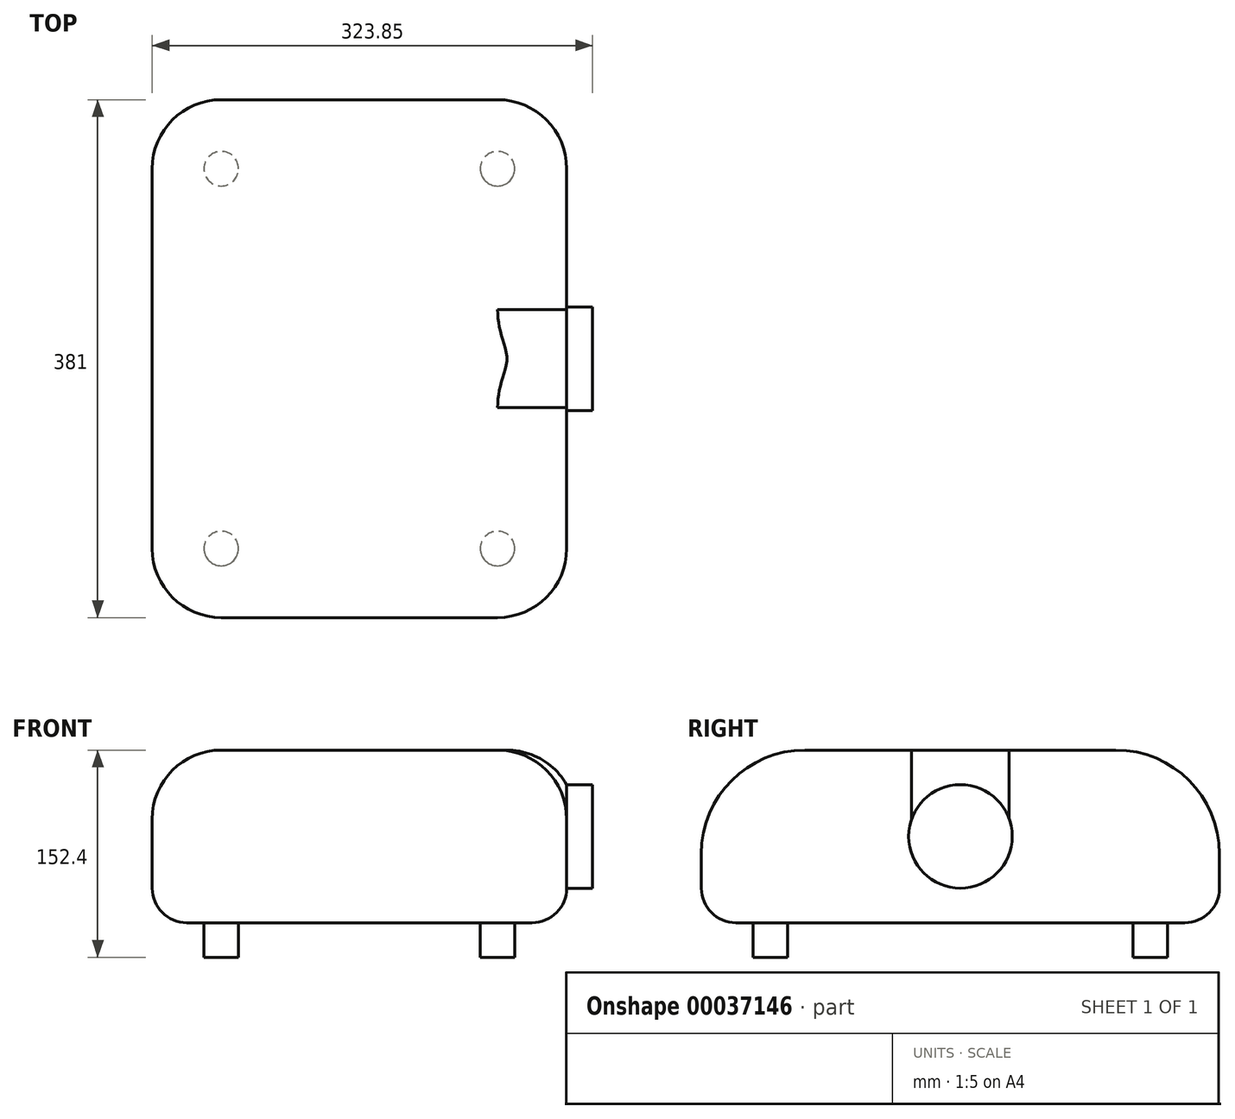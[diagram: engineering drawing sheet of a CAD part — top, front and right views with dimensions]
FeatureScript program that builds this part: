
annotation { "Feature Type Name" : "Feature", "Feature Type Description" : "" }
export const myFeature = defineFeature(function(context is Context, id is Id, definition is map)
    precondition{}
    {
        {
            var Q0;
            Q0=qCreatedBy(makeId("Top.planeOp"),FACE);
            var sketch = newSketch(context, id + "F0", { "sketchPlane" : qUnion([Q0])});
            skLineSegment(sketch, "E0.bottom", {"start": v(-168.65, 186.98) * mm, "end": v(136.15, 186.98) * mm});
            skLineSegment(sketch, "E0.top", {"start": v(-168.65, -194.02) * mm, "end": v(136.15, -194.02) * mm});
            skLineSegment(sketch, "E0.left", {"start": v(-168.65, 186.98) * mm, "end": v(-168.65, -194.02) * mm});
            skLineSegment(sketch, "E0.right", {"start": v(136.15, 186.98) * mm, "end": v(136.15, -194.02) * mm});
            skSolve(sketch);
        }
        {
            var Q0;
            Q0 = qSketchRegion(id + "F0", true);
            extrude(context, id + "F1", {"entities" : qUnion([Q0]), "depth" : 127 * mm});
        }
        {
            var Q0;
            Q0=makeQuery(id+"F1.opExtrude","CAP_FACE",FACE,{"disambiguationData":[OSD([sQuery(id+"F0.wireOp",EDGE,"E0.bottom"),sQuery(id+"F0.wireOp",EDGE,"E0.top"),sQuery(id+"F0.wireOp",EDGE,"E0.left"),sQuery(id+"F0.wireOp",EDGE,"E0.right")])],"isStart":true});
            var sketch = newSketch(context, id + "F2", { "sketchPlane" : qUnion([Q0])});
            skCircle(sketch, "E1", {"center": v(-117.85, -136.18) * mm, "radius": 12.7 * mm});
            skCircle(sketch, "E2", {"center": v(-117.85, 143.22) * mm, "radius": 12.7 * mm});
            skCircle(sketch, "E3", {"center": v(85.35, 143.22) * mm, "radius": 12.7 * mm});
            skCircle(sketch, "E4", {"center": v(85.35, -136.18) * mm, "radius": 12.7 * mm});
            skSolve(sketch);
        }
        {
            var Q0;
            Q0 = qSketchRegion(id + "F2", true);
            extrude(context, id + "F3", {"entities" : qUnion([Q0]), "operationType" : NewBodyOperationType.ADD, "depth" : 25.4 * mm});
        }
        {
            var Q0;
            Q0=makeQuery(id+"F1.opExtrude","CAP_EDGE",EDGE,{"disambiguationData":[OSD([sQuery(id+"F0.wireOp",EDGE,"E0.bottom")])],"isStart":false});
            var Q1;
            Q1=makeQuery(id+"F1.opExtrude","CAP_EDGE",EDGE,{"disambiguationData":[OSD([sQuery(id+"F0.wireOp",EDGE,"E0.top")])],"isStart":false});
            fillet(context, id + "F4", {"entities" : qUnion([Q0, Q1]), "radius" : 76.2 * mm, "tangentPropagation" : true, "allowEdgeOverflow" : false});
        }
        {
            var Q0;
            Q0=makeQuery(id+"F1.opExtrude","SWEPT_FACE",FACE,{"disambiguationData":[OSD([sQuery(id+"F0.wireOp",EDGE,"E0.right")])]});
            var sketch = newSketch(context, id + "F5", { "sketchPlane" : qUnion([Q0])});
            skCircle(sketch, "E5", {"center": v(-3.52, 63.5) * mm, "radius": 38.1 * mm});
            skPoint(sketch, "E5.centerSnap0", {"position": v(-3.52, 76.2) * mm});
            skSolve(sketch);
        }
        {
            var Q0;
            Q0 = qSketchRegion(id + "F5", true);
            extrude(context, id + "F6", {"entities" : qUnion([Q0]), "operationType" : NewBodyOperationType.ADD, "depth" : 19.05 * mm, "hasSecondDirection" : true, "secondDirectionOppositeDirection" : true, "secondDirectionDepth" : 25.4 * mm});
        }
        {
            var Q0;
            Q0=makeQuery(id+"F1.opExtrude","CAP_EDGE",EDGE,{"disambiguationData":[OSD([sQuery(id+"F0.wireOp",EDGE,"E0.right")])],"isStart":false});
            var Q1;
            Q1=makeQuery(id+"F1.opExtrude","CAP_EDGE",EDGE,{"disambiguationData":[OSD([sQuery(id+"F0.wireOp",EDGE,"E0.left")])],"isStart":false});
            fillet(context, id + "F7", {"entities" : qUnion([Q0, Q1]), "radius" : 50.8 * mm, "tangentPropagation" : true, "allowEdgeOverflow" : false});
        }
        {
            var Q0;
            Q0=makeQuery(id+"F1.opExtrude","CAP_EDGE",EDGE,{"disambiguationData":[OSD([sQuery(id+"F0.wireOp",EDGE,"E0.bottom")])],"isStart":true});
            fillet(context, id + "F8", {"entities" : qUnion([Q0]), "radius" : 25.4 * mm, "tangentPropagation" : true, "allowEdgeOverflow" : false});
        }
    });
